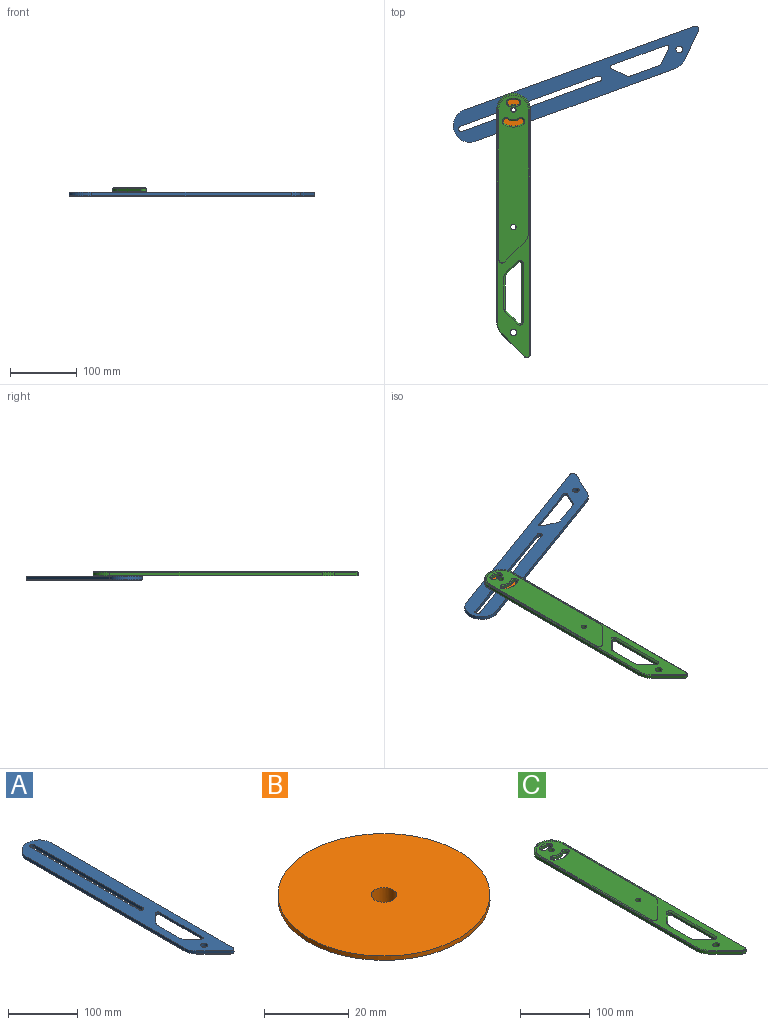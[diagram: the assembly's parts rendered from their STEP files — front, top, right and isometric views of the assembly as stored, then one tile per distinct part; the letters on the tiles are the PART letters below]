
ASSEMBLY  parts=3 mates=2
PART A: 35 faces, bbox 50x397.5x6 mm
  f0: plane 220x6mm, normal (-1,0,0), area 1320mm2, adj f1,f13,f14,f15
  f1: cylinder r=4mm len=8mm, axis (0,0,1), area 75.4mm2, adj f0,f2,f14,f15
  f2: plane 220x6mm, normal (1,0,0), area 1320mm2, adj f1,f13,f14,f15
  f3: plane 87.11x4mm, normal (-1,0,0), area 348.5mm2, adj f15,f16,f17,f26
  f4: plane 17.54x17.54mm, normal (0.71,-0.71,0), area 99.2mm2, adj f15,f16,f18,f29
  f5: plane 44.97x4mm, normal (1,0,0), area 179.9mm2, adj f15,f18,f19,f33
  f6: cylinder r=25mm len=50mm, axis (0,0,1), area 392.7mm2, adj f7,f12,f15,f21
  f7: plane 367.53x5mm, normal (1,0,0), area 1837.6mm2, adj f6,f8,f15,f23
  f8: cylinder r=5mm len=8.54mm, axis (0,0,1), area 58.9mm2, adj f7,f9,f15,f25
  f9: plane 34.14x34.14mm, normal (-0.71,-0.71,0), area 241.4mm2, adj f8,f10,f15,f24
  f10: cylinder r=25mm len=17.68mm, axis (0,0,1), area 98.2mm2, adj f9,f12,f15,f22
  f11: plane 17.54x17.54mm, normal (0.71,0.71,0), area 99.2mm2, adj f15,f17,f19,f30
  f12: plane 319.24x5mm, normal (-1,0,0), area 1596.2mm2, adj f6,f10,f15,f20
  f13: cylinder r=4mm len=8mm, axis (0,0,1), area 75.4mm2, adj f0,f2,f14,f15
  f14: plane 395.53x48mm, normal (0,0,-1), area 13617.4mm2, adj f0,f1,f2,f13,f20,f21,f22,f23
  f15: plane 397.53x50mm, normal (0,0,1), area 14888.6mm2, adj f0,f1,f2,f3,f4,f5,f6,f7
  f16: cylinder r=3mm len=5.12mm, axis (0,0,-1), area 28.3mm2, adj f3,f4,f15,f27
  f17: cylinder r=3mm len=5.12mm, axis (0,0,-1), area 28.3mm2, adj f3,f11,f15,f28
  f18: cylinder r=8mm len=5.66mm, axis (0,0,-1), area 25.1mm2, adj f4,f5,f15,f31
  f19: cylinder r=8mm len=5.66mm, axis (0,0,-1), area 25.1mm2, adj f5,f11,f15,f32
  f20: plane 319.24x1mm, normal (-0.71,0,-0.71), area 451.5mm2, adj f12,f14,f21,f22
  f21: cone r=25mm half-angle=45deg, axis (0,0,1), area 108.9mm2, adj f6,f14,f20,f23
  f22: cone r=24mm half-angle=45deg, axis (0,0,1), area 27.2mm2, adj f10,f14,f20,f24
  f23: plane 367.53x1mm, normal (0.71,0,-0.71), area 519.8mm2, adj f7,f14,f21,f25
  f24: plane 34.85x34.85mm, normal (-0.5,-0.5,-0.71), area 68.3mm2, adj f9,f14,f22,f25
  f25: cone r=4mm half-angle=45deg, axis (0,0,1), area 15mm2, adj f8,f14,f23,f24
  f26: plane 87.11x2mm, normal (-0.71,0,-0.71), area 246.4mm2, adj f3,f14,f27,f28
  f27: cone r=5mm half-angle=45deg, axis (0,0,-1), area 26.7mm2, adj f14,f16,f26,f29
  f28: cone r=5mm half-angle=45deg, axis (0,0,-1), area 26.7mm2, adj f14,f17,f26,f30
  f29: plane 18.95x18.95mm, normal (0.5,-0.5,-0.71), area 70.1mm2, adj f4,f14,f27,f31
  f30: plane 18.95x18.95mm, normal (0.5,0.5,-0.71), area 70.1mm2, adj f11,f14,f28,f32
  f31: cone r=10mm half-angle=45deg, axis (0,0,-1), area 20mm2, adj f14,f18,f29,f33
  f32: cone r=10mm half-angle=45deg, axis (0,0,-1), area 20mm2, adj f14,f19,f30,f33
  f33: plane 44.97x2mm, normal (0.71,0,-0.71), area 127.2mm2, adj f5,f14,f31,f32
  f34: cylinder r=5mm len=10mm, axis (0,0,1), area 188.5mm2, adj f14,f15
PART B: 9 faces, bbox 50x50x7.3 mm
  f0: plane 50x50mm, normal (0,0,1), area 1935.2mm2, adj f2,f3
  f1: plane 50x50mm, normal (0,0,-1), area 1705.2mm2, adj f3,f5,f6,f7,f8
  f2: cylinder r=3mm len=7.25mm, axis (0,0,-1), area 136.7mm2, adj f0,f4
  f3: cylinder r=25mm len=50mm, axis (0,0,-1), area 196.3mm2, adj f0,f1
  f4: plane 34x8mm, normal (0,0,-1), area 230mm2, adj f2,f5,f6,f7,f8
  f5: cylinder r=4mm len=8mm, axis (0,0,1), area 75.4mm2, adj f1,f4,f6,f8
  f6: plane 26x6mm, normal (1,0,0), area 156mm2, adj f1,f4,f5,f7
  f7: cylinder r=4mm len=8mm, axis (0,0,1), area 75.4mm2, adj f1,f4,f6,f8
  f8: plane 26x6mm, normal (-1,0,0), area 156mm2, adj f1,f4,f5,f7
PART C: 56 faces, bbox 50x397.5x6 mm
  f0: cylinder r=4mm len=8mm, axis (0,0,-1), area 138.2mm2, adj f11,f53
  f1: cone r=6mm half-angle=45deg, axis (0,0,1), area 31.7mm2, adj f2,f3,f29,f53
  f2: cone r=6mm half-angle=45deg, axis (0,0,-1), area 13.7mm2, adj f1,f4,f24,f53
  f3: cone r=16mm half-angle=45deg, axis (0,0,1), area 31.7mm2, adj f1,f4,f25,f53
  f4: cone r=6mm half-angle=45deg, axis (0,0,1), area 31.7mm2, adj f2,f3,f28,f53
  f5: cone r=6mm half-angle=45deg, axis (0,0,1), area 31.7mm2, adj f6,f7,f27,f53
  f6: cone r=24.5mm half-angle=45deg, axis (0,0,1), area 63.1mm2, adj f5,f8,f23,f53
  f7: cone r=14.5mm half-angle=45deg, axis (0,0,-1), area 39.4mm2, adj f5,f8,f22,f53
  f8: cone r=6mm half-angle=45deg, axis (0,0,1), area 31.7mm2, adj f6,f7,f26,f53
  f9: cylinder r=4mm len=8mm, axis (0,0,1), area 138.2mm2, adj f11,f53
  f10: plane 395.53x48mm, normal (0,0,1), area 5239.3mm2, adj f34,f35,f36,f37,f38,f39,f40,f41
  f11: plane 397.53x50mm, normal (0,0,-1), area 16219.1mm2, adj f0,f9,f12,f13,f14,f15,f16,f17
  f12: plane 87.11x4mm, normal (-1,0,0), area 348.5mm2, adj f11,f30,f31,f34
  f13: plane 17.54x17.54mm, normal (0.71,0.71,0), area 99.2mm2, adj f11,f30,f32,f38
  f14: plane 44.97x4mm, normal (1,0,0), area 179.9mm2, adj f11,f32,f33,f41
  f15: plane 367.53x5mm, normal (1,0,0), area 1837.6mm2, adj f11,f16,f21,f46
  f16: cylinder r=25mm len=50mm, axis (0,0,-1), area 392.7mm2, adj f11,f15,f17,f44
  f17: plane 319.24x5mm, normal (-1,0,0), area 1596.2mm2, adj f11,f16,f18,f42
  f18: cylinder r=25mm len=17.68mm, axis (0,0,-1), area 98.2mm2, adj f11,f17,f19,f43
  f19: plane 34.14x34.14mm, normal (-0.71,-0.71,0), area 241.4mm2, adj f11,f18,f21,f45
  f20: plane 17.54x17.54mm, normal (0.71,-0.71,0), area 99.2mm2, adj f11,f31,f33,f37
  f21: cylinder r=5mm len=8.54mm, axis (0,0,-1), area 58.9mm2, adj f11,f15,f19,f47
  f22: cylinder r=16.5mm len=18.33mm, axis (0,0,1), area 77.8mm2, adj f7,f11,f26,f27
  f23: cylinder r=24.5mm len=27.22mm, axis (0,0,1), area 115.4mm2, adj f6,f11,f26,f27
  f24: cylinder r=8mm len=6.9mm, axis (0,0,1), area 28.5mm2, adj f2,f11,f28,f29
  f25: cylinder r=16mm len=13.79mm, axis (0,0,1), area 57mm2, adj f3,f11,f28,f29
  f26: cylinder r=4mm len=7.33mm, axis (0,0,1), area 50.3mm2, adj f8,f11,f22,f23
  f27: cylinder r=4mm len=7.33mm, axis (0,0,1), area 50.3mm2, adj f5,f11,f22,f23
  f28: cylinder r=4mm len=7.61mm, axis (0,0,1), area 50.3mm2, adj f4,f11,f24,f25
  f29: cylinder r=4mm len=7.61mm, axis (0,0,1), area 50.3mm2, adj f1,f11,f24,f25
  f30: cylinder r=3mm len=5.12mm, axis (0,0,1), area 28.3mm2, adj f11,f12,f13,f36
  f31: cylinder r=3mm len=5.12mm, axis (0,0,1), area 28.3mm2, adj f11,f12,f20,f35
  f32: cylinder r=8mm len=5.66mm, axis (0,0,1), area 25.1mm2, adj f11,f13,f14,f40
  f33: cylinder r=8mm len=5.66mm, axis (0,0,1), area 25.1mm2, adj f11,f14,f20,f39
  f34: plane 87.11x2mm, normal (-0.71,0,0.71), area 246.4mm2, adj f10,f12,f35,f36
  f35: cone r=5mm half-angle=45deg, axis (0,0,1), area 26.7mm2, adj f10,f31,f34,f37
  f36: cone r=5mm half-angle=45deg, axis (0,0,1), area 26.7mm2, adj f10,f30,f34,f38
  f37: plane 18.95x18.95mm, normal (0.5,-0.5,0.71), area 70.1mm2, adj f10,f20,f35,f39
  f38: plane 18.95x18.95mm, normal (0.5,0.5,0.71), area 70.1mm2, adj f10,f13,f36,f40
  f39: cone r=10mm half-angle=45deg, axis (0,0,1), area 20mm2, adj f10,f33,f37,f41
  f40: cone r=10mm half-angle=45deg, axis (0,0,1), area 20mm2, adj f10,f32,f38,f41
  f41: plane 44.97x2mm, normal (0.71,0,0.71), area 127.2mm2, adj f10,f14,f39,f40
  f42: plane 319.24x1mm, normal (-0.71,0,0.71), area 451.5mm2, adj f10,f17,f43,f44
  f43: cone r=24mm half-angle=45deg, axis (0,0,-1), area 27.2mm2, adj f10,f18,f42,f45
  f44: cone r=24mm half-angle=45deg, axis (0,0,-1), area 108.9mm2, adj f10,f16,f42,f46
  f45: plane 34.85x34.85mm, normal (-0.5,-0.5,0.71), area 68.3mm2, adj f10,f19,f43,f47
  f46: plane 367.53x1mm, normal (0.71,0,0.71), area 519.8mm2, adj f10,f15,f44,f47
  f47: cone r=4mm half-angle=45deg, axis (0,0,-1), area 15mm2, adj f10,f21,f45,f46
  f48: cylinder r=5mm len=10mm, axis (0,0,1), area 188.5mm2, adj f10,f11
  f49: plane 31.07x31.07mm, normal (-0.71,0.71,0), area 22mm2, adj f10,f53,f54,f55
  f50: plane 186.87x0.5mm, normal (-1,0,0), area 93.4mm2, adj f10,f51,f53,f54
  f51: cylinder r=22mm len=44mm, axis (0,0,1), area 34.6mm2, adj f10,f50,f52,f53
  f52: plane 225.02x0.5mm, normal (1,0,0), area 112.5mm2, adj f10,f51,f53,f55
  f53: plane 252.02x44mm, normal (0,0,1), area 9514.5mm2, adj f0,f1,f2,f3,f4,f5,f6,f7
  f54: cylinder r=15mm len=10.61mm, axis (0,0,-1), area 5.9mm2, adj f10,f49,f50,f53
  f55: cylinder r=5mm len=8.54mm, axis (0,0,-1), area 5.9mm2, adj f10,f49,f52,f53
PLACE A rot(axis=(0,0,1),110deg) t=(-65.39,-23.8,0)mm
PLACE B rot(axis=(0,0,-1),70deg) t=(0,0,0)mm
PLACE C at identity fixed
MATE pin_slot B.f7 <-> A.f1  axis (0,0,-1) through (12.22,4.45,-7)mm
MATE revolute B.f2 <-> C.f0  axis (0,0,1) through (0,0,0.25)mm
